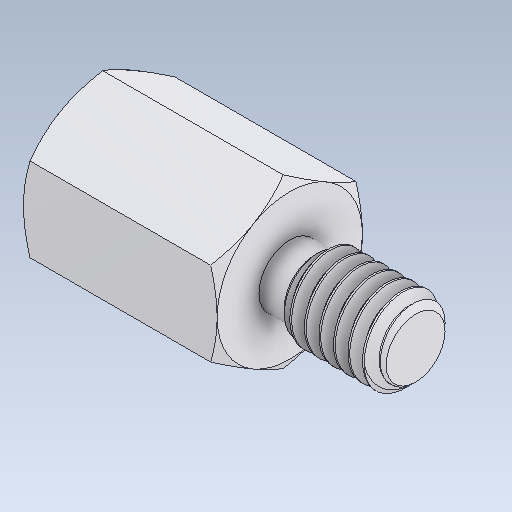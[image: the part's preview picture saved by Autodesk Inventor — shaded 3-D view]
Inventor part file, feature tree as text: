
AUTODESK INVENTOR PART (.ipt)
format: ipt  version: 2021 (Build 250183000, 183)  size: 513,536 bytes
history: native  units: in
note: dims shown in document units (in); Inventor stores cm internally (conversion verified against a paired STEP export)
features: extrude x1
ambient origin geometry x8: Origin, YZ Plane, XZ Plane, XY Plane, X Axis, Y Axis, Z Axis, Center Point
bodies: Solid1 (feature_tree)
feature tree (1):
  extrude  "Extrude8"  [1 undecoded]
note: 1 required parameter value undecoded (feature->parameter linkage not recoverable at this tier; creation-order binding heuristic only, values carry confidence <= 0.55)
